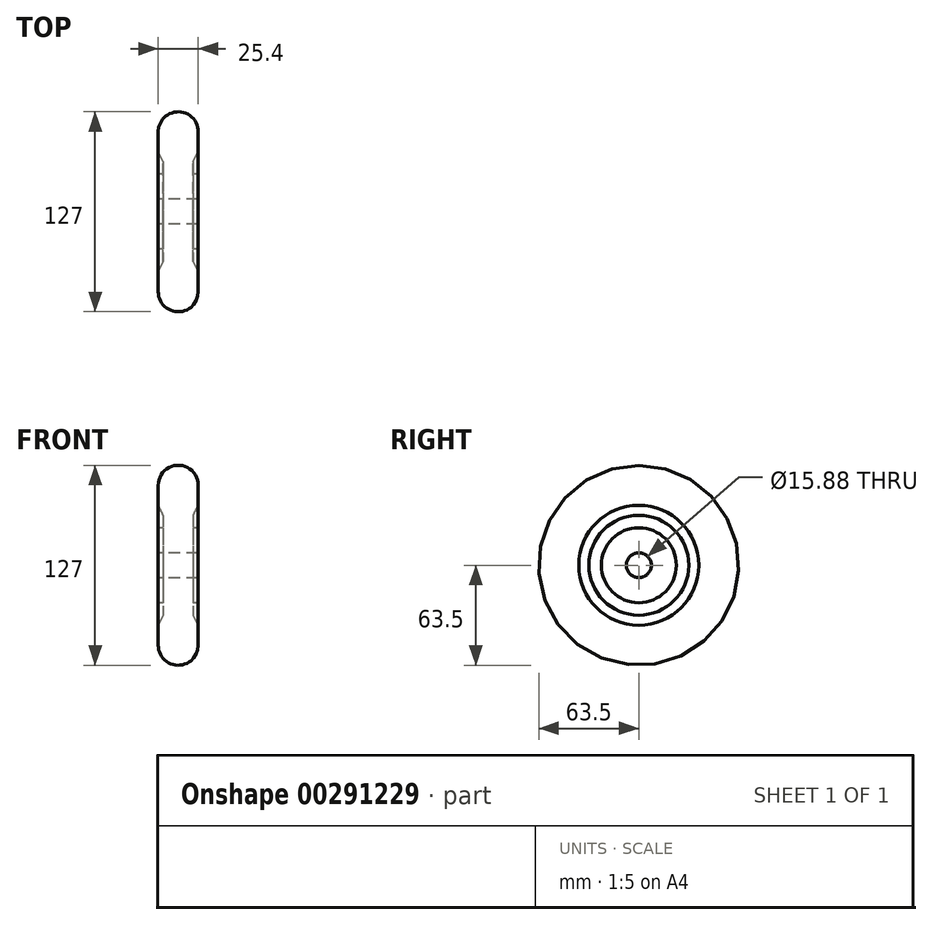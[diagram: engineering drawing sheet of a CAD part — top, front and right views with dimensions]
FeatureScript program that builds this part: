
annotation { "Feature Type Name" : "Feature", "Feature Type Description" : "" }
export const myFeature = defineFeature(function(context is Context, id is Id, definition is map)
    precondition{}
    {
        {
            var Q0;
            Q0=qCreatedBy(makeId("Front.planeOp"),FACE);
            var sketch = newSketch(context, id + "F0", { "sketchPlane" : qUnion([Q0])});
            skLineSegment(sketch, "E0", {"start": v(0, 7.94) * mm, "end": v(12.7, 7.94) * mm});
            skLineSegment(sketch, "E1", {"start": v(12.7, 7.94) * mm, "end": v(12.7, 23.81) * mm});
            skLineSegment(sketch, "E2", {"start": v(12.7, 23.81) * mm, "end": v(9.52, 23.81) * mm});
            skLineSegment(sketch, "E3", {"start": v(9.52, 23.81) * mm, "end": v(9.52, 31.75) * mm});
            skLineSegment(sketch, "E4", {"start": v(9.52, 31.75) * mm, "end": v(12.7, 38.1) * mm});
            skLineSegment(sketch, "E5", {"start": v(12.7, 38.1) * mm, "end": v(12.7, 50.8) * mm});
            skArc(sketch, "E6", {"start": v(12.7, 50.8) * mm, "mid": v(8.98, 59.78) * mm, "end": v(0, 63.5) * mm});
            skLineSegment(sketch, "E7", {"start": v(0, 0) * mm, "end": v(0, 81.16) * mm, "construction": true});
            skLineSegment(sketch, "E8.MirrorCS", {"start": v(-12.7, 23.81) * mm, "end": v(-9.52, 23.81) * mm});
            skLineSegment(sketch, "E9.MirrorCS", {"start": v(-9.52, 31.75) * mm, "end": v(-12.7, 38.1) * mm});
            skLineSegment(sketch, "E10.MirrorCS", {"start": v(-9.52, 23.81) * mm, "end": v(-9.52, 31.75) * mm});
            skLineSegment(sketch, "E11.MirrorCS", {"start": v(0, 7.94) * mm, "end": v(-12.7, 7.94) * mm});
            skLineSegment(sketch, "E12.MirrorCS", {"start": v(-12.7, 7.94) * mm, "end": v(-12.7, 23.81) * mm});
            skLineSegment(sketch, "E13.MirrorCS", {"start": v(-12.7, 38.1) * mm, "end": v(-12.7, 50.8) * mm});
            skArc(sketch, "E14.MirrorCS", {"start": v(-12.7, 50.8) * mm, "mid": v(-8.98, 59.78) * mm, "end": v(0, 63.5) * mm});
            skLineSegment(sketch, "E15", {"start": v(-96.88, 0) * mm, "end": v(90.34, 0) * mm, "construction": true});
            skSolve(sketch);
        }
        {
            var Q0;
            Q0 = qSketchRegion(id + "F0", true);
            var Q1;
            Q1=sQuery(id+"F0.wireOp",EDGE,"E15");
            revolve(context, id + "F1", {"entities" : qUnion([Q0]), "axis" : qUnion([Q1]), "revolveType" : RevolveType.FULL});
        }
    });
